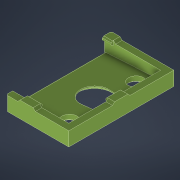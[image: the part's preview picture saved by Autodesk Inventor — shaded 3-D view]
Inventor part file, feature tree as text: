
AUTODESK INVENTOR PART (.ipt)
format: ipt  version: 2022.1 (Build 261234000, 234)  size: 467,968 bytes
history: native  units: mm
features: sketch x25, extrude x24, projected_geometry x13, chamfer x11, fillet x7, other x3, plane x1, hole x1, reference x1
ambient origin geometry x8: Origin, YZ Plane, XZ Plane, XY Plane, X Axis, Y Axis, Z Axis, Center Point
bodies: Volumenkörper1 (feature_tree)
feature tree (86):
  extrude  "Extrusion1"  Depth=21.0mm
  extrude  "Extrusion2"  Depth=16.03mm
  chamfer  "Fase1"  Distance=2.0mm
  extrude  "Extrusion3"  Depth=19.3mm
  extrude  "Extrusion4"  Depth=1.7mm TaperAngle=0.0deg
  extrude  "Extrusion5"  Depth=3.5mm
  extrude  "Extrusion6"  Depth=0.3mm
  extrude  "Extrusion7"  Depth=0.8mm
  chamfer  "Fase2"  Distance=0.8mm
  chamfer  "Fase4"  Distance=1.0mm
  fillet  "Rundung3"  Radius=0.3mm
  extrude  "Extrusion8"  Depth=1.5mm
  chamfer  "Fase5"  Distance=0.8mm
  fillet  "Rundung4"  Radius=0.3mm
  extrude  "Extrusion9"  Depth=0.5mm TaperAngle=45.0deg
  chamfer  "Fase6"  Distance=2.0mm
  extrude  "Extrusion10"  Depth=10.0mm
  extrude  "Extrusion11"  Depth=10.0mm TaperAngle=0.0deg
  chamfer  "Fase7"  Distance=1.0mm
  chamfer  "Fase8"  Distance=0.5mm Angle=45.0deg
  fillet  "Rundung6"  Radius=0.6mm
  chamfer  "Fase9"  Distance=0.3mm
  fillet  "Rundung7"  Radius=0.2mm
  plane  "Arbeitsebene1"
  extrude  "Extrusion14"  Depth=10.0mm
  sketch  "Skizze15"  dims[d24=0.0mm d25=0.0mm d26=0.3mm]
  extrude  "Extrusion15"  TaperAngle=0.0deg  [1 undecoded]
  hole  "Bohrung2"  [1 undecoded]
  extrude  "Extrusion16"  Depth=10.0mm TaperAngle=0.0deg
  sketch  "Skizze18"  dims[d29=3.0mm]
  extrude  "Extrusion18"  Depth=10.0mm
  extrude  "Extrusion19"  TaperAngle=180.0deg  [1 undecoded]
  extrude  "Extrusion20"  Depth=10.0mm
  extrude  "Extrusion21"  Depth=10.0mm
  extrude  "Extrusion22"  Depth=10.0mm TaperAngle=0.0deg
  extrude  "Extrusion23"  Depth=10.0mm TaperAngle=0.0deg
  extrude  "Extrusion24"  Depth=10.0mm
  chamfer  "Fase11"  Distance=0.5mm
  extrude  "Extrusion25"  Depth=10.0mm TaperAngle=0.0deg
  extrude  "Extrusion26"  Depth=10.0mm TaperAngle=0.0deg
  fillet  "Rundung10"  Radius=0.5mm
  extrude  "Extrusion27"  Depth=10.0mm
  fillet  "Rundung12"  Radius=0.5mm
  fillet  "Rundung13"  Radius=1.5mm
  chamfer  "Fase12"  Distance=0.5mm
  chamfer  "Fase13"  Distance=0.5mm
  sketch  "Skizze1"  dims[d0=16.3mm d1=21.0mm]
  sketch  "Skizze2"  dims[d2=2.0mm d3=0.0mm d4=16.03mm]
  sketch  "Skizze3"  dims[d5=20.54mm]
  sketch  "Skizze4"  dims[d6=13.35mm]
  projected_geometry  "Projizierte Kontur1"
  sketch  "Skizze5"  dims[d7=7.6mm]
  sketch  "Skizze6"  dims[d8=90.0deg]
  sketch  "Skizze7"  dims[d9=15.2mm]
  projected_geometry  "Projizierte Kontur2"
  sketch  "Skizze8"  dims[d10=3.0mm]
  sketch  "Skizze9"  dims[d11=3.0mm d12=2.0mm d13=0.0mm]
  projected_geometry  "Projizierte Kontur3"
  sketch  "Skizze10"  dims[d14=0.5mm d15=2.0mm d16=45.0deg d17=19.3mm]
  sketch  "Skizze11"  dims[d18=24.0mm d19=1.7mm d20=0.0mm]
  projected_geometry  "Projizierte Kontur4"
  sketch  "Skizze14"  dims[d21=1.0mm d22=0.0mm d23=3.5mm]
  sketch  "Skizze17"  dims[d27=90.0deg d28=0.8mm]
  reference  "Referenz2"
  projected_geometry  "Projizierte Kontur9"
  sketch  "Skizze19"  dims[d30=0.8mm d31=0.8mm d32=0.0mm d33=1.0mm d34=0.0mm]
  sketch  "Skizze20"  dims[d35=0.5mm d36=2.0mm d37=45.0deg]
  projected_geometry  "Projizierte Kontur10"
  sketch  "Skizze21"  dims[d43=0.6mm d44=2.0mm d45=45.0deg d46=0.3mm]
  projected_geometry  "Projizierte Kontur11"
  sketch  "Skizze22"  dims[d47=0.3mm d48=1.5mm]
  projected_geometry  "Projizierte Kontur12"
  sketch  "Skizze23"  dims[d49=0.8mm]
  projected_geometry  "Projizierte Kontur13"
  sketch  "Skizze24"  dims[d50=1.5mm d51=0.8mm d52=0.0mm]
  projected_geometry  "Projizierte Kontur14"
  sketch  "Skizze25"  dims[d53=0.6mm d54=2.0mm d55=45.0deg d56=0.3mm]
  projected_geometry  "Projizierte Kontur15"
  sketch  "Skizze26"  dims[d57=1.0mm d58=0.0mm d59=0.5mm d60=2.0mm d61=45.0deg]
  projected_geometry  "Projizierte Kontur16"
  sketch  "Skizze27"  dims[d62=2.0mm]
  projected_geometry  "Projizierte Kontur17"
  sketch  "Skizze28"  dims[d63=0.3mm d64=2.0mm d65=0.5mm d66=0.8mm d67=0.0mm d68=1.0mm d69=0.0mm d70=0.5mm d71=2.0mm d72=45.0deg d73=0.6mm d74=2.0mm d75=45.0deg d77=0.3mm d78=0.2mm d79=2.0mm d80=45.0deg d81=1.0mm d91=0.0mm d92=0.0mm d93=0.5mm d94=0.0mm d102=3.3mm d103=6.0mm d104=6.3mm d105=2.0mm d106=90.0deg d107=8.0mm d108=20.594885mm d109=0.5mm d110=0.0mm d111=2.7mm d112=180.0deg d113=5.4mm d123=5.0mm d124=0.5mm d125=0.0mm d126=0.5mm d127=0.0mm d128=3.6mm d129=0.5mm d130=0.0mm d131=0.5mm d132=0.0mm d133=1.0mm d134=0.0mm d135=0.5mm d136=0.0mm d137=9.0mm d138=0.5mm d139=0.0mm d140=1.5mm d141=2.0mm d142=45.0deg d143=0.5mm d144=0.0mm d146=0.5mm d147=0.0mm d148=2.0mm d150=30.805061mm d151=10.0mm d152=0.0mm d153=0.1mm d154=0.3mm d155=0.3mm d156=2.0mm d157=45.0deg d158=0.2mm d159=2.0mm d160=45.0deg]
  other  "<userpath>\Desktop\DragonHF\Combined.iam"
  other  "Combined.iam"
  other  "TriangleLab_Clip:1"
note: 3 required parameter values undecoded (feature->parameter linkage not recoverable at this tier; creation-order binding heuristic only, values carry confidence <= 0.55)
